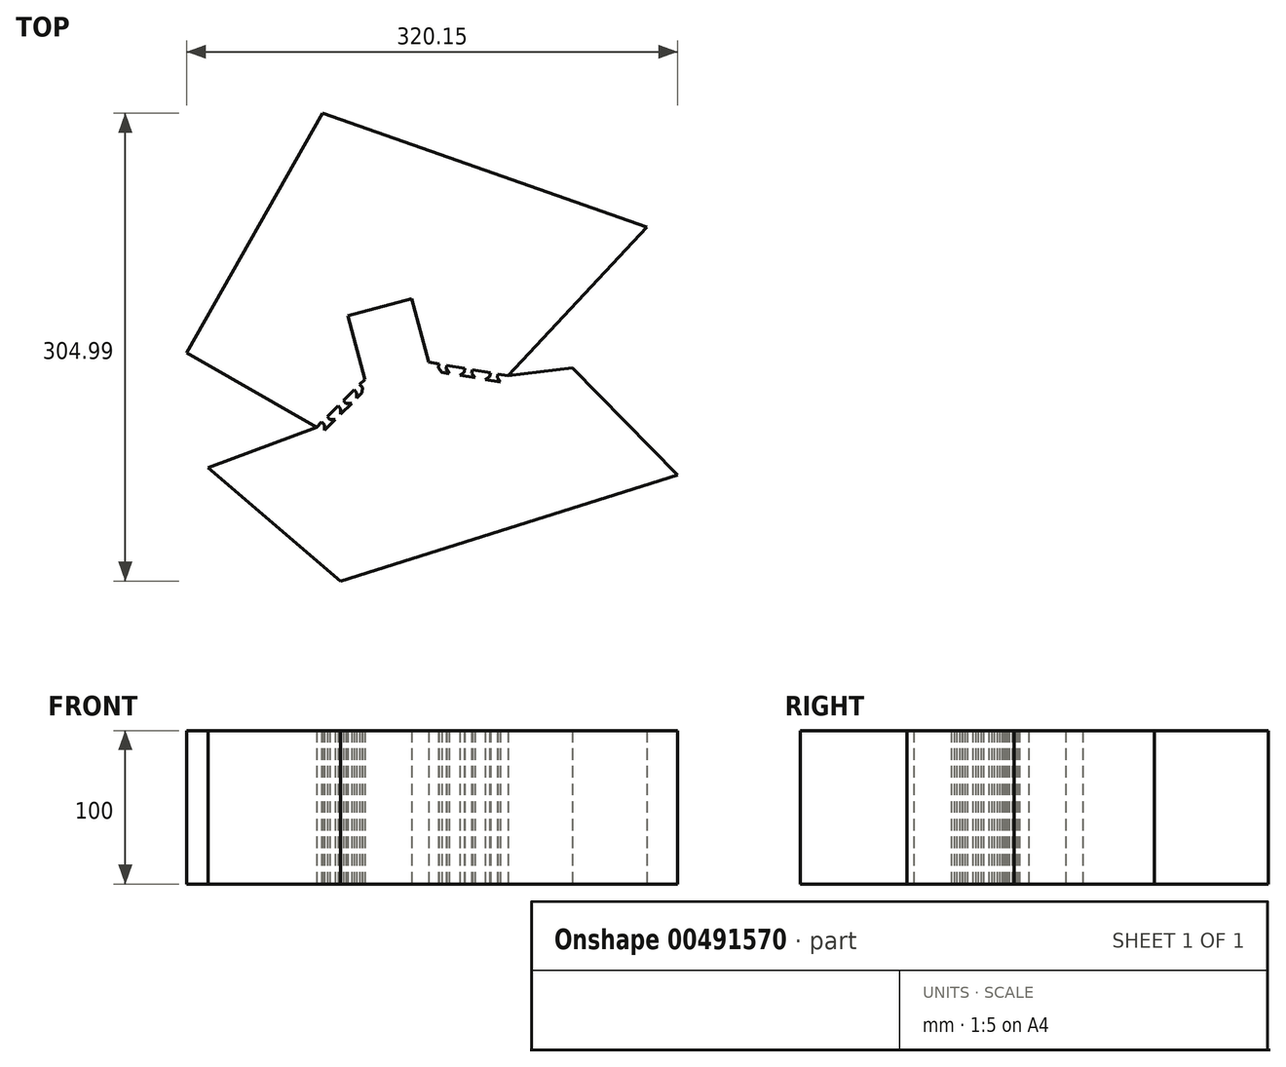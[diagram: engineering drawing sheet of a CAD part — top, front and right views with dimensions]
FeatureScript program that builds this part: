
annotation { "Feature Type Name" : "Feature", "Feature Type Description" : "" }
export const myFeature = defineFeature(function(context is Context, id is Id, definition is map)
    precondition{}
    {
        {
            var Q0;
            Q0=qCreatedBy(makeId("Top.planeOp"),FACE);
            var sketch = newSketch(context, id + "F0", { "sketchPlane" : qUnion([Q0])});
            skLineSegment(sketch, "E0", {"start": v(13.23, -95.22) * mm, "end": v(4.45, -92.87) * mm});
            skLineSegment(sketch, "E1", {"start": v(4.45, -92.87) * mm, "end": v(14.84, -54.1) * mm});
            skLineSegment(sketch, "E2", {"start": v(14.84, -54.1) * mm, "end": v(52.07, -64.07) * mm});
            skLineSegment(sketch, "E3", {"start": v(52.07, -64.07) * mm, "end": v(52.62, -63.48) * mm});
            skLineSegment(sketch, "E4", {"start": v(52.62, -63.48) * mm, "end": v(64.97, -66.78) * mm});
            skLineSegment(sketch, "E5", {"start": v(64.97, -66.78) * mm, "end": v(69.57, -49.62) * mm});
            skLineSegment(sketch, "E6", {"start": v(69.57, -49.62) * mm, "end": v(71.06, -48.58) * mm});
            skLineSegment(sketch, "E7", {"start": v(71.06, -48.58) * mm, "end": v(72.55, -48.7) * mm});
            skLineSegment(sketch, "E8", {"start": v(72.55, -48.7) * mm, "end": v(81.24, -48.85) * mm});
            skLineSegment(sketch, "E9", {"start": v(81.24, -48.85) * mm, "end": v(89.36, -48.18) * mm});
            skLineSegment(sketch, "E10", {"start": v(89.36, -48.18) * mm, "end": v(92.14, -47.5) * mm});
            skLineSegment(sketch, "E11", {"start": v(92.14, -47.5) * mm, "end": v(93.87, -41.05) * mm});
            skLineSegment(sketch, "E12", {"start": v(93.87, -41.05) * mm, "end": v(93.82, -41.03) * mm});
            skLineSegment(sketch, "E13", {"start": v(93.82, -41.03) * mm, "end": v(95.53, -34.66) * mm});
            skLineSegment(sketch, "E14", {"start": v(95.53, -34.66) * mm, "end": v(95.58, -34.67) * mm});
            skLineSegment(sketch, "E15", {"start": v(95.58, -34.67) * mm, "end": v(97.3, -28.22) * mm});
            skLineSegment(sketch, "E16", {"start": v(97.3, -28.22) * mm, "end": v(95.23, -26.24) * mm});
            skLineSegment(sketch, "E17", {"start": v(95.23, -26.24) * mm, "end": v(88.55, -21.6) * mm});
            skLineSegment(sketch, "E18", {"start": v(88.55, -21.6) * mm, "end": v(80.94, -17.38) * mm});
            skLineSegment(sketch, "E19", {"start": v(80.94, -17.38) * mm, "end": v(79.6, -16.74) * mm});
            skLineSegment(sketch, "E20", {"start": v(79.6, -16.74) * mm, "end": v(77.01, -11.2) * mm});
            skLineSegment(sketch, "E21", {"start": v(77.01, -11.2) * mm, "end": v(72.37, -13.37) * mm});
            skLineSegment(sketch, "E22", {"start": v(72.37, -13.37) * mm, "end": v(65.9, -10.6) * mm});
            skLineSegment(sketch, "E23", {"start": v(65.9, -10.6) * mm, "end": v(59.65, -8) * mm});
            skLineSegment(sketch, "E24", {"start": v(59.65, -8) * mm, "end": v(54.72, -5.74) * mm});
            skLineSegment(sketch, "E25", {"start": v(54.72, -5.74) * mm, "end": v(53.87, -5.26) * mm});
            skLineSegment(sketch, "E26", {"start": v(53.87, -5.26) * mm, "end": v(54.52, -3.42) * mm});
            skLineSegment(sketch, "E27", {"start": v(54.52, -3.42) * mm, "end": v(55.5, -0.95) * mm});
            skLineSegment(sketch, "E28", {"start": v(55.5, -0.95) * mm, "end": v(57.7, 4.32) * mm});
            skLineSegment(sketch, "E29", {"start": v(57.7, 4.32) * mm, "end": v(58.83, 7.13) * mm});
            skLineSegment(sketch, "E30", {"start": v(58.83, 7.13) * mm, "end": v(59.9, 10.04) * mm});
            skLineSegment(sketch, "E31", {"start": v(59.9, 10.04) * mm, "end": v(60.84, 13.05) * mm});
            skLineSegment(sketch, "E32", {"start": v(60.84, 13.05) * mm, "end": v(61.6, 16.13) * mm});
            skLineSegment(sketch, "E33", {"start": v(61.6, 16.13) * mm, "end": v(62.15, 19.25) * mm});
            skLineSegment(sketch, "E34", {"start": v(62.15, 19.25) * mm, "end": v(62.43, 22.38) * mm});
            skLineSegment(sketch, "E35", {"start": v(62.43, 22.38) * mm, "end": v(62.4, 25.48) * mm});
            skLineSegment(sketch, "E36", {"start": v(62.4, 25.48) * mm, "end": v(62.03, 28.51) * mm});
            skLineSegment(sketch, "E37", {"start": v(62.03, 28.51) * mm, "end": v(61.65, 30.08) * mm});
            skLineSegment(sketch, "E38", {"start": v(61.65, 30.08) * mm, "end": v(56.95, 31.97) * mm});
            skLineSegment(sketch, "E39", {"start": v(56.95, 31.97) * mm, "end": v(54.45, 32.5) * mm});
            skLineSegment(sketch, "E40", {"start": v(54.45, 32.5) * mm, "end": v(54.48, 32.63) * mm});
            skLineSegment(sketch, "E41", {"start": v(54.48, 32.63) * mm, "end": v(53.29, 33.7) * mm});
            skLineSegment(sketch, "E42", {"start": v(53.29, 33.7) * mm, "end": v(53.62, 35.26) * mm});
            skLineSegment(sketch, "E43", {"start": v(53.62, 35.26) * mm, "end": v(55.14, 35.76) * mm});
            skLineSegment(sketch, "E44", {"start": v(55.14, 35.76) * mm, "end": v(55.33, 35.6) * mm});
            skLineSegment(sketch, "E45", {"start": v(55.33, 35.6) * mm, "end": v(57.89, 35.05) * mm});
            skLineSegment(sketch, "E46", {"start": v(57.89, 35.05) * mm, "end": v(60.28, 34.08) * mm});
            skLineSegment(sketch, "E47", {"start": v(60.28, 34.08) * mm, "end": v(60.23, 34.2) * mm});
            skLineSegment(sketch, "E48", {"start": v(60.23, 34.2) * mm, "end": v(58.8, 36.78) * mm});
            skLineSegment(sketch, "E49", {"start": v(58.8, 36.78) * mm, "end": v(57.03, 39.14) * mm});
            skLineSegment(sketch, "E50", {"start": v(57.03, 39.14) * mm, "end": v(54.94, 41.25) * mm});
            skLineSegment(sketch, "E51", {"start": v(54.94, 41.25) * mm, "end": v(52.56, 43.1) * mm});
            skLineSegment(sketch, "E52", {"start": v(52.56, 43.1) * mm, "end": v(49.94, 44.66) * mm});
            skLineSegment(sketch, "E53", {"start": v(49.94, 44.66) * mm, "end": v(47.12, 45.96) * mm});
            skLineSegment(sketch, "E54", {"start": v(47.12, 45.96) * mm, "end": v(44.15, 46.98) * mm});
            skLineSegment(sketch, "E55", {"start": v(44.15, 46.98) * mm, "end": v(41.07, 47.75) * mm});
            skLineSegment(sketch, "E56", {"start": v(41.07, 47.75) * mm, "end": v(37.95, 48.3) * mm});
            skLineSegment(sketch, "E57", {"start": v(37.95, 48.3) * mm, "end": v(34.82, 48.66) * mm});
            skLineSegment(sketch, "E58", {"start": v(34.82, 48.66) * mm, "end": v(31.72, 48.87) * mm});
            skLineSegment(sketch, "E59", {"start": v(31.72, 48.87) * mm, "end": v(28.7, 48.99) * mm});
            skLineSegment(sketch, "E60", {"start": v(28.7, 48.99) * mm, "end": v(23, 49.11) * mm});
            skLineSegment(sketch, "E61", {"start": v(23, 49.11) * mm, "end": v(20.34, 49.22) * mm});
            skLineSegment(sketch, "E62", {"start": v(20.34, 49.22) * mm, "end": v(17.82, 49.43) * mm});
            skLineSegment(sketch, "E63", {"start": v(17.82, 49.43) * mm, "end": v(15.44, 49.77) * mm});
            skLineSegment(sketch, "E64", {"start": v(15.44, 49.77) * mm, "end": v(13.2, 50.28) * mm});
            skLineSegment(sketch, "E65", {"start": v(13.2, 50.28) * mm, "end": v(11.05, 50.98) * mm});
            skLineSegment(sketch, "E66", {"start": v(11.05, 50.98) * mm, "end": v(8.98, 51.9) * mm});
            skLineSegment(sketch, "E67", {"start": v(8.98, 51.9) * mm, "end": v(6.96, 53.02) * mm});
            skLineSegment(sketch, "E68", {"start": v(6.96, 53.02) * mm, "end": v(4.97, 54.36) * mm});
            skLineSegment(sketch, "E69", {"start": v(4.97, 54.36) * mm, "end": v(2.97, 55.9) * mm});
            skLineSegment(sketch, "E70", {"start": v(2.97, 55.9) * mm, "end": v(0.92, 57.59) * mm});
            skLineSegment(sketch, "E71", {"start": v(0.92, 57.59) * mm, "end": v(-3.4, 61.31) * mm});
            skLineSegment(sketch, "E72", {"start": v(-3.4, 61.31) * mm, "end": v(-5.73, 63.25) * mm});
            skLineSegment(sketch, "E73", {"start": v(-5.73, 63.25) * mm, "end": v(-8.17, 65.16) * mm});
            skLineSegment(sketch, "E74", {"start": v(-8.17, 65.16) * mm, "end": v(-10.74, 66.99) * mm});
            skLineSegment(sketch, "E75", {"start": v(-10.74, 66.99) * mm, "end": v(-13.4, 68.66) * mm});
            skLineSegment(sketch, "E76", {"start": v(-13.4, 68.66) * mm, "end": v(-16.2, 75.2) * mm});
            skLineSegment(sketch, "E77", {"start": v(-16.2, 75.2) * mm, "end": v(-14.04, 79.84) * mm});
            skLineSegment(sketch, "E78", {"start": v(-14.04, 79.84) * mm, "end": v(-19.57, 82.42) * mm});
            skLineSegment(sketch, "E79", {"start": v(-19.57, 82.42) * mm, "end": v(-20.2, 83.77) * mm});
            skLineSegment(sketch, "E80", {"start": v(-20.2, 83.77) * mm, "end": v(-24.43, 91.38) * mm});
            skLineSegment(sketch, "E81", {"start": v(-24.43, 91.38) * mm, "end": v(-29.07, 98.06) * mm});
            skLineSegment(sketch, "E82", {"start": v(-29.07, 98.06) * mm, "end": v(-31.05, 100.13) * mm});
            skLineSegment(sketch, "E83", {"start": v(-31.05, 100.13) * mm, "end": v(-37.5, 98.4) * mm});
            skLineSegment(sketch, "E84", {"start": v(-37.5, 98.4) * mm, "end": v(-37.49, 98.36) * mm});
            skLineSegment(sketch, "E85", {"start": v(-37.49, 98.36) * mm, "end": v(-43.86, 96.65) * mm});
            skLineSegment(sketch, "E86", {"start": v(-43.86, 96.65) * mm, "end": v(-43.88, 96.7) * mm});
            skLineSegment(sketch, "E87", {"start": v(-43.88, 96.7) * mm, "end": v(-50.32, 94.97) * mm});
            skLineSegment(sketch, "E88", {"start": v(-50.32, 94.97) * mm, "end": v(-51, 92.19) * mm});
            skLineSegment(sketch, "E89", {"start": v(-51, 92.19) * mm, "end": v(-51.68, 84.07) * mm});
            skLineSegment(sketch, "E90", {"start": v(-51.68, 84.07) * mm, "end": v(-51.53, 75.38) * mm});
            skLineSegment(sketch, "E91", {"start": v(-51.53, 75.38) * mm, "end": v(-51.4, 73.9) * mm});
            skLineSegment(sketch, "E92", {"start": v(-51.4, 73.9) * mm, "end": v(-54.91, 68.89) * mm});
            skLineSegment(sketch, "E93", {"start": v(-54.91, 68.89) * mm, "end": v(-50.4, 65.73) * mm});
            skLineSegment(sketch, "E94", {"start": v(-50.4, 65.73) * mm, "end": v(-48.9, 67.88) * mm});
            skLineSegment(sketch, "E95", {"start": v(-48.9, 67.88) * mm, "end": v(-42.35, 43.42) * mm});
            skLineSegment(sketch, "E96", {"start": v(-42.35, 43.42) * mm, "end": v(-51.04, 41.1) * mm});
            skLineSegment(sketch, "E97", {"start": v(-51.04, 41.1) * mm, "end": v(-53.64, 50.8) * mm});
            skLineSegment(sketch, "E98", {"start": v(-53.64, 50.8) * mm, "end": v(-53.81, 50.37) * mm});
            skLineSegment(sketch, "E99", {"start": v(-53.81, 50.37) * mm, "end": v(-54.85, 47.53) * mm});
            skLineSegment(sketch, "E100", {"start": v(-54.85, 47.53) * mm, "end": v(-56.74, 42.14) * mm});
            skLineSegment(sketch, "E101", {"start": v(-56.74, 42.14) * mm, "end": v(-57.66, 39.65) * mm});
            skLineSegment(sketch, "E102", {"start": v(-57.66, 39.65) * mm, "end": v(-58.63, 37.32) * mm});
            skLineSegment(sketch, "E103", {"start": v(-58.63, 37.32) * mm, "end": v(-59.7, 35.16) * mm});
            skLineSegment(sketch, "E104", {"start": v(-59.7, 35.16) * mm, "end": v(-60.87, 33.18) * mm});
            skLineSegment(sketch, "E105", {"start": v(-60.87, 33.18) * mm, "end": v(-62.2, 31.35) * mm});
            skLineSegment(sketch, "E106", {"start": v(-62.2, 31.35) * mm, "end": v(-63.71, 29.67) * mm});
            skLineSegment(sketch, "E107", {"start": v(-63.71, 29.67) * mm, "end": v(-65.4, 28.1) * mm});
            skLineSegment(sketch, "E108", {"start": v(-65.4, 28.1) * mm, "end": v(-67.3, 26.62) * mm});
            skLineSegment(sketch, "E109", {"start": v(-67.3, 26.62) * mm, "end": v(-69.37, 25.19) * mm});
            skLineSegment(sketch, "E110", {"start": v(-69.37, 25.19) * mm, "end": v(-71.62, 23.76) * mm});
            skLineSegment(sketch, "E111", {"start": v(-71.62, 23.76) * mm, "end": v(-76.5, 20.8) * mm});
            skLineSegment(sketch, "E112", {"start": v(-76.5, 20.8) * mm, "end": v(-79.06, 19.2) * mm});
            skLineSegment(sketch, "E113", {"start": v(-79.06, 19.2) * mm, "end": v(-81.63, 17.46) * mm});
            skLineSegment(sketch, "E114", {"start": v(-81.63, 17.46) * mm, "end": v(-84.16, 15.58) * mm});
            skLineSegment(sketch, "E115", {"start": v(-84.16, 15.58) * mm, "end": v(-86.6, 13.54) * mm});
            skLineSegment(sketch, "E116", {"start": v(-86.6, 13.54) * mm, "end": v(-88.87, 11.34) * mm});
            skLineSegment(sketch, "E117", {"start": v(-88.87, 11.34) * mm, "end": v(-90.93, 8.96) * mm});
            skLineSegment(sketch, "E118", {"start": v(-90.93, 8.96) * mm, "end": v(-92.73, 6.44) * mm});
            skLineSegment(sketch, "E119", {"start": v(-92.73, 6.44) * mm, "end": v(-94.22, 3.77) * mm});
            skLineSegment(sketch, "E120", {"start": v(-94.22, 3.77) * mm, "end": v(-94.82, 2.28) * mm});
            skLineSegment(sketch, "E121", {"start": v(-94.82, 2.28) * mm, "end": v(-92.14, -2.02) * mm});
            skLineSegment(sketch, "E122", {"start": v(-92.14, -2.02) * mm, "end": v(-90.43, -3.92) * mm});
            skLineSegment(sketch, "E123", {"start": v(-90.43, -3.92) * mm, "end": v(-90.52, -4) * mm});
            skLineSegment(sketch, "E124", {"start": v(-90.52, -4) * mm, "end": v(-90.19, -5.56) * mm});
            skLineSegment(sketch, "E125", {"start": v(-90.19, -5.56) * mm, "end": v(-91.38, -6.63) * mm});
            skLineSegment(sketch, "E126", {"start": v(-91.38, -6.63) * mm, "end": v(-92.9, -6.14) * mm});
            skLineSegment(sketch, "E127", {"start": v(-92.9, -6.14) * mm, "end": v(-92.95, -5.9) * mm});
            skLineSegment(sketch, "E128", {"start": v(-92.95, -5.9) * mm, "end": v(-94.7, -3.95) * mm});
            skLineSegment(sketch, "E129", {"start": v(-94.7, -3.95) * mm, "end": v(-96.07, -1.76) * mm});
            skLineSegment(sketch, "E130", {"start": v(-96.07, -1.76) * mm, "end": v(-96.1, -1.9) * mm});
            skLineSegment(sketch, "E131", {"start": v(-96.1, -1.9) * mm, "end": v(-96.46, -4.82) * mm});
            skLineSegment(sketch, "E132", {"start": v(-96.46, -4.82) * mm, "end": v(-96.41, -7.77) * mm});
            skLineSegment(sketch, "E133", {"start": v(-96.41, -7.77) * mm, "end": v(-95.96, -10.7) * mm});
            skLineSegment(sketch, "E134", {"start": v(-95.96, -10.7) * mm, "end": v(-95.13, -13.6) * mm});
            skLineSegment(sketch, "E135", {"start": v(-95.13, -13.6) * mm, "end": v(-93.93, -16.4) * mm});
            skLineSegment(sketch, "E136", {"start": v(-93.93, -16.4) * mm, "end": v(-92.4, -19.1) * mm});
            skLineSegment(sketch, "E137", {"start": v(-92.4, -19.1) * mm, "end": v(-90.6, -21.68) * mm});
            skLineSegment(sketch, "E138", {"start": v(-90.6, -21.68) * mm, "end": v(-88.57, -24.11) * mm});
            skLineSegment(sketch, "E139", {"start": v(-88.57, -24.11) * mm, "end": v(-86.36, -26.4) * mm});
            skLineSegment(sketch, "E140", {"start": v(-86.36, -26.4) * mm, "end": v(-84.04, -28.53) * mm});
            skLineSegment(sketch, "E141", {"start": v(-84.04, -28.53) * mm, "end": v(-81.66, -30.52) * mm});
            skLineSegment(sketch, "E142", {"start": v(-81.66, -30.52) * mm, "end": v(-79.29, -32.39) * mm});
            skLineSegment(sketch, "E143", {"start": v(-79.29, -32.39) * mm, "end": v(-74.74, -35.84) * mm});
            skLineSegment(sketch, "E144", {"start": v(-74.74, -35.84) * mm, "end": v(-72.66, -37.5) * mm});
            skLineSegment(sketch, "E145", {"start": v(-72.66, -37.5) * mm, "end": v(-71.18, -38.76) * mm});
            skLineSegment(sketch, "E146", {"start": v(-71.18, -38.76) * mm, "end": v(-71.67, -39.6) * mm});
            skLineSegment(sketch, "E147", {"start": v(-71.67, -39.6) * mm, "end": v(-74.81, -44.02) * mm});
            skLineSegment(sketch, "E148", {"start": v(-74.81, -44.02) * mm, "end": v(-78.92, -49.4) * mm});
            skLineSegment(sketch, "E149", {"start": v(-78.92, -49.4) * mm, "end": v(-83.14, -55.04) * mm});
            skLineSegment(sketch, "E150", {"start": v(-83.14, -55.04) * mm, "end": v(-88.24, -55.49) * mm});
            skLineSegment(sketch, "E151", {"start": v(-88.24, -55.49) * mm, "end": v(-87.7, -61.57) * mm});
            skLineSegment(sketch, "E152", {"start": v(-87.7, -61.57) * mm, "end": v(-88.56, -62.8) * mm});
            skLineSegment(sketch, "E153", {"start": v(-88.56, -62.8) * mm, "end": v(-93.03, -70.25) * mm});
            skLineSegment(sketch, "E154", {"start": v(-93.03, -70.25) * mm, "end": v(-96.5, -77.61) * mm});
            skLineSegment(sketch, "E155", {"start": v(-96.5, -77.61) * mm, "end": v(-97.3, -80.37) * mm});
            skLineSegment(sketch, "E156", {"start": v(-97.3, -80.37) * mm, "end": v(-92.58, -85.09) * mm});
            skLineSegment(sketch, "E157", {"start": v(-92.58, -85.09) * mm, "end": v(-92.55, -85.05) * mm});
            skLineSegment(sketch, "E158", {"start": v(-92.55, -85.05) * mm, "end": v(-87.88, -89.72) * mm});
            skLineSegment(sketch, "E159", {"start": v(-87.88, -89.72) * mm, "end": v(-87.92, -89.75) * mm});
            skLineSegment(sketch, "E160", {"start": v(-87.92, -89.75) * mm, "end": v(-83.2, -94.47) * mm});
            skLineSegment(sketch, "E161", {"start": v(-83.2, -94.47) * mm, "end": v(-80.44, -93.67) * mm});
            skLineSegment(sketch, "E162", {"start": v(-80.44, -93.67) * mm, "end": v(-73.08, -90.2) * mm});
            skLineSegment(sketch, "E163", {"start": v(-73.08, -90.2) * mm, "end": v(-65.63, -85.73) * mm});
            skLineSegment(sketch, "E164", {"start": v(-65.63, -85.73) * mm, "end": v(-64.4, -84.88) * mm});
            skLineSegment(sketch, "E165", {"start": v(-64.4, -84.88) * mm, "end": v(-58.32, -85.4) * mm});
            skLineSegment(sketch, "E166", {"start": v(-58.32, -85.4) * mm, "end": v(-57.87, -80.31) * mm});
            skLineSegment(sketch, "E167", {"start": v(-57.87, -80.31) * mm, "end": v(-54.33, -77.66) * mm});
            skLineSegment(sketch, "E168", {"start": v(-54.33, -77.66) * mm, "end": v(-53.76, -78.62) * mm});
            skLineSegment(sketch, "E169", {"start": v(-53.76, -78.62) * mm, "end": v(-51.9, -81.1) * mm});
            skLineSegment(sketch, "E170", {"start": v(-51.9, -81.1) * mm, "end": v(-49.83, -83.35) * mm});
            skLineSegment(sketch, "E171", {"start": v(-49.83, -83.35) * mm, "end": v(-48.6, -84.38) * mm});
            skLineSegment(sketch, "E172", {"start": v(-48.6, -84.38) * mm, "end": v(-43.69, -83.16) * mm});
            skLineSegment(sketch, "E173", {"start": v(-43.69, -83.16) * mm, "end": v(-41.35, -82.12) * mm});
            skLineSegment(sketch, "E174", {"start": v(-41.35, -82.12) * mm, "end": v(-41.3, -82.23) * mm});
            skLineSegment(sketch, "E175", {"start": v(-41.3, -82.23) * mm, "end": v(-39.71, -82.4) * mm});
            skLineSegment(sketch, "E176", {"start": v(-39.71, -82.4) * mm, "end": v(-39.06, -83.86) * mm});
            skLineSegment(sketch, "E177", {"start": v(-39.06, -83.86) * mm, "end": v(-40, -85.16) * mm});
            skLineSegment(sketch, "E178", {"start": v(-40, -85.16) * mm, "end": v(-40.25, -85.13) * mm});
            skLineSegment(sketch, "E179", {"start": v(-40.25, -85.13) * mm, "end": v(-42.64, -86.2) * mm});
            skLineSegment(sketch, "E180", {"start": v(-42.64, -86.2) * mm, "end": v(-45.15, -86.82) * mm});
            skLineSegment(sketch, "E181", {"start": v(-45.15, -86.82) * mm, "end": v(-45.03, -86.9) * mm});
            skLineSegment(sketch, "E182", {"start": v(-45.03, -86.9) * mm, "end": v(-42.36, -88.14) * mm});
            skLineSegment(sketch, "E183", {"start": v(-42.36, -88.14) * mm, "end": v(-39.54, -89) * mm});
            skLineSegment(sketch, "E184", {"start": v(-39.54, -89) * mm, "end": v(-36.6, -89.48) * mm});
            skLineSegment(sketch, "E185", {"start": v(-36.6, -89.48) * mm, "end": v(-33.6, -89.58) * mm});
            skLineSegment(sketch, "E186", {"start": v(-33.6, -89.58) * mm, "end": v(-30.56, -89.3) * mm});
            skLineSegment(sketch, "E187", {"start": v(-30.56, -89.3) * mm, "end": v(-27.52, -88.7) * mm});
            skLineSegment(sketch, "E188", {"start": v(-27.52, -88.7) * mm, "end": v(-24.5, -87.77) * mm});
            skLineSegment(sketch, "E189", {"start": v(-24.5, -87.77) * mm, "end": v(-21.57, -86.59) * mm});
            skLineSegment(sketch, "E190", {"start": v(-21.57, -86.59) * mm, "end": v(-18.72, -85.2) * mm});
            skLineSegment(sketch, "E191", {"start": v(-18.72, -85.2) * mm, "end": v(-15.97, -83.65) * mm});
            skLineSegment(sketch, "E192", {"start": v(-15.97, -83.65) * mm, "end": v(-13.34, -82) * mm});
            skLineSegment(sketch, "E193", {"start": v(-13.34, -82) * mm, "end": v(-10.83, -80.32) * mm});
            skLineSegment(sketch, "E194", {"start": v(-10.83, -80.32) * mm, "end": v(-6.14, -77.06) * mm});
            skLineSegment(sketch, "E195", {"start": v(-6.14, -77.06) * mm, "end": v(-3.93, -75.6) * mm});
            skLineSegment(sketch, "E196", {"start": v(-3.93, -75.6) * mm, "end": v(-1.89, -74.35) * mm});
            skLineSegment(sketch, "E197", {"start": v(-1.89, -74.35) * mm, "end": v(-7.4, -94.96) * mm});
            skLineSegment(sketch, "E198", {"start": v(-7.4, -94.96) * mm, "end": v(11.9, -100.13) * mm});
            skLineSegment(sketch, "E199", {"start": v(11.9, -100.13) * mm, "end": v(13.23, -95.22) * mm});
            skLineSegment(sketch, "E200", {"start": v(-41.07, 86.22) * mm, "end": v(-40.95, 86.25) * mm});
            skLineSegment(sketch, "E201", {"start": v(-40.95, 86.25) * mm, "end": v(-41, 86.4) * mm});
            skLineSegment(sketch, "E202", {"start": v(-41, 86.4) * mm, "end": v(-40.82, 86.6) * mm});
            skLineSegment(sketch, "E203", {"start": v(-40.82, 86.6) * mm, "end": v(-40.84, 86.65) * mm});
            skLineSegment(sketch, "E204", {"start": v(-40.84, 86.65) * mm, "end": v(-40.6, 86.96) * mm});
            skLineSegment(sketch, "E205", {"start": v(-40.6, 86.96) * mm, "end": v(-40.35, 87.03) * mm});
            skLineSegment(sketch, "E206", {"start": v(-40.35, 87.03) * mm, "end": v(-40.38, 87.13) * mm});
            skLineSegment(sketch, "E207", {"start": v(-40.38, 87.13) * mm, "end": v(-40.05, 87.5) * mm});
            skLineSegment(sketch, "E208", {"start": v(-40.05, 87.5) * mm, "end": v(-39.59, 87.77) * mm});
            skLineSegment(sketch, "E209", {"start": v(-39.59, 87.77) * mm, "end": v(-39.3, 86.7) * mm});
            skLineSegment(sketch, "E210", {"start": v(-39.3, 86.7) * mm, "end": v(-36.46, 87.46) * mm});
            skLineSegment(sketch, "E211", {"start": v(-36.46, 87.46) * mm, "end": v(-36.75, 88.53) * mm});
            skLineSegment(sketch, "E212", {"start": v(-36.75, 88.53) * mm, "end": v(-36.74, 88.53) * mm});
            skLineSegment(sketch, "E213", {"start": v(-36.74, 88.53) * mm, "end": v(-36.58, 88.55) * mm});
            skLineSegment(sketch, "E214", {"start": v(-36.58, 88.55) * mm, "end": v(-35.94, 88.47) * mm});
            skLineSegment(sketch, "E215", {"start": v(-35.94, 88.47) * mm, "end": v(-35.7, 88.27) * mm});
            skLineSegment(sketch, "E216", {"start": v(-35.7, 88.27) * mm, "end": v(-35.47, 88.34) * mm});
            skLineSegment(sketch, "E217", {"start": v(-35.47, 88.34) * mm, "end": v(-35.06, 88.17) * mm});
            skLineSegment(sketch, "E218", {"start": v(-35.06, 88.17) * mm, "end": v(-35.06, 88.15) * mm});
            skLineSegment(sketch, "E219", {"start": v(-35.06, 88.15) * mm, "end": v(-34.77, 87.91) * mm});
            skLineSegment(sketch, "E220", {"start": v(-34.77, 87.91) * mm, "end": v(-34.7, 87.93) * mm});
            skLineSegment(sketch, "E221", {"start": v(-34.7, 87.93) * mm, "end": v(-32.05, 78.07) * mm});
            skLineSegment(sketch, "E222", {"start": v(-32.05, 78.07) * mm, "end": v(-38.43, 76.36) * mm});
            skLineSegment(sketch, "E223", {"start": v(-38.43, 76.36) * mm, "end": v(-41.07, 86.22) * mm});
            skLineSegment(sketch, "E224", {"start": v(22.96, 40.54) * mm, "end": v(23.69, 41.96) * mm});
            skLineSegment(sketch, "E225", {"start": v(23.69, 41.96) * mm, "end": v(23.8, 41.97) * mm});
            skLineSegment(sketch, "E226", {"start": v(23.8, 41.97) * mm, "end": v(25.7, 43.2) * mm});
            skLineSegment(sketch, "E227", {"start": v(25.7, 43.2) * mm, "end": v(29.94, 45.36) * mm});
            skLineSegment(sketch, "E228", {"start": v(29.94, 45.36) * mm, "end": v(34.37, 47.06) * mm});
            skLineSegment(sketch, "E229", {"start": v(34.37, 47.06) * mm, "end": v(36.66, 47.67) * mm});
            skLineSegment(sketch, "E230", {"start": v(36.66, 47.67) * mm, "end": v(37.49, 44.58) * mm});
            skLineSegment(sketch, "E231", {"start": v(37.49, 44.58) * mm, "end": v(35.36, 44.01) * mm});
            skLineSegment(sketch, "E232", {"start": v(35.36, 44.01) * mm, "end": v(31.24, 42.43) * mm});
            skLineSegment(sketch, "E233", {"start": v(31.24, 42.43) * mm, "end": v(27.31, 40.43) * mm});
            skLineSegment(sketch, "E234", {"start": v(27.31, 40.43) * mm, "end": v(25.46, 39.23) * mm});
            skLineSegment(sketch, "E235", {"start": v(25.46, 39.23) * mm, "end": v(25.43, 39.28) * mm});
            skLineSegment(sketch, "E236", {"start": v(25.43, 39.28) * mm, "end": v(23.83, 39.2) * mm});
            skLineSegment(sketch, "E237", {"start": v(23.83, 39.2) * mm, "end": v(22.96, 40.54) * mm});
            skLineSegment(sketch, "E238", {"start": v(-50.75, 33.92) * mm, "end": v(-9.15, 45.07) * mm});
            skLineSegment(sketch, "E239", {"start": v(-9.15, 45.07) * mm, "end": v(1.98, 3.54) * mm});
            skLineSegment(sketch, "E240", {"start": v(1.94, 3.5) * mm, "end": v(-39.66, -7.65) * mm});
            skLineSegment(sketch, "E241", {"start": v(-39.62, -7.6) * mm, "end": v(-50.75, 33.92) * mm});
            skLineSegment(sketch, "E242", {"start": v(32.15, 6.18) * mm, "end": v(28.9, 7.43) * mm});
            skLineSegment(sketch, "E243", {"start": v(28.9, 7.43) * mm, "end": v(25.98, 9.33) * mm});
            skLineSegment(sketch, "E244", {"start": v(25.98, 9.33) * mm, "end": v(23.52, 11.8) * mm});
            skLineSegment(sketch, "E245", {"start": v(23.52, 11.8) * mm, "end": v(21.62, 14.71) * mm});
            skLineSegment(sketch, "E246", {"start": v(21.62, 14.71) * mm, "end": v(20.37, 17.97) * mm});
            skLineSegment(sketch, "E247", {"start": v(20.37, 17.97) * mm, "end": v(19.82, 21.4) * mm});
            skLineSegment(sketch, "E248", {"start": v(19.82, 21.4) * mm, "end": v(20, 24.89) * mm});
            skLineSegment(sketch, "E249", {"start": v(20, 24.89) * mm, "end": v(20.9, 28.25) * mm});
            skLineSegment(sketch, "E250", {"start": v(20.9, 28.25) * mm, "end": v(22.5, 31.36) * mm});
            skLineSegment(sketch, "E251", {"start": v(22.5, 31.36) * mm, "end": v(24.68, 34.06) * mm});
            skLineSegment(sketch, "E252", {"start": v(24.68, 34.06) * mm, "end": v(27.4, 36.26) * mm});
            skLineSegment(sketch, "E253", {"start": v(27.4, 36.26) * mm, "end": v(30.5, 37.84) * mm});
            skLineSegment(sketch, "E254", {"start": v(30.5, 37.84) * mm, "end": v(33.86, 38.74) * mm});
            skLineSegment(sketch, "E255", {"start": v(33.86, 38.74) * mm, "end": v(37.34, 38.92) * mm});
            skLineSegment(sketch, "E256", {"start": v(37.34, 38.92) * mm, "end": v(40.78, 38.38) * mm});
            skLineSegment(sketch, "E257", {"start": v(40.78, 38.38) * mm, "end": v(44.03, 37.13) * mm});
            skLineSegment(sketch, "E258", {"start": v(44.03, 37.13) * mm, "end": v(46.96, 35.23) * mm});
            skLineSegment(sketch, "E259", {"start": v(46.96, 35.23) * mm, "end": v(49.42, 32.77) * mm});
            skLineSegment(sketch, "E260", {"start": v(49.42, 32.77) * mm, "end": v(51.32, 29.85) * mm});
            skLineSegment(sketch, "E261", {"start": v(51.32, 29.85) * mm, "end": v(52.57, 26.6) * mm});
            skLineSegment(sketch, "E262", {"start": v(52.57, 26.6) * mm, "end": v(53.11, 23.15) * mm});
            skLineSegment(sketch, "E263", {"start": v(53.11, 23.15) * mm, "end": v(52.93, 19.67) * mm});
            skLineSegment(sketch, "E264", {"start": v(52.93, 19.67) * mm, "end": v(52.03, 16.3) * mm});
            skLineSegment(sketch, "E265", {"start": v(52.03, 16.3) * mm, "end": v(50.45, 13.2) * mm});
            skLineSegment(sketch, "E266", {"start": v(50.45, 13.2) * mm, "end": v(48.25, 10.5) * mm});
            skLineSegment(sketch, "E267", {"start": v(48.25, 10.5) * mm, "end": v(45.55, 8.3) * mm});
            skLineSegment(sketch, "E268", {"start": v(45.55, 8.3) * mm, "end": v(42.44, 6.72) * mm});
            skLineSegment(sketch, "E269", {"start": v(42.44, 6.72) * mm, "end": v(39.08, 5.82) * mm});
            skLineSegment(sketch, "E270", {"start": v(39.08, 5.82) * mm, "end": v(35.6, 5.64) * mm});
            skLineSegment(sketch, "E271", {"start": v(35.6, 5.64) * mm, "end": v(32.15, 6.18) * mm});
            skLineSegment(sketch, "E272", {"start": v(-70.15, 14.9) * mm, "end": v(-70.07, 16.5) * mm});
            skLineSegment(sketch, "E273", {"start": v(-70.07, 16.5) * mm, "end": v(-68.64, 17.22) * mm});
            skLineSegment(sketch, "E274", {"start": v(-68.64, 17.22) * mm, "end": v(-67.3, 16.35) * mm});
            skLineSegment(sketch, "E275", {"start": v(-67.3, 16.35) * mm, "end": v(-67.38, 14.76) * mm});
            skLineSegment(sketch, "E276", {"start": v(-67.38, 14.76) * mm, "end": v(-68.8, 14.03) * mm});
            skLineSegment(sketch, "E277", {"start": v(-68.8, 14.03) * mm, "end": v(-70.15, 14.9) * mm});
            skLineSegment(sketch, "E278", {"start": v(-74.18, -22.31) * mm, "end": v(-77.44, -21.06) * mm});
            skLineSegment(sketch, "E279", {"start": v(-77.44, -21.06) * mm, "end": v(-80.36, -19.17) * mm});
            skLineSegment(sketch, "E280", {"start": v(-80.36, -19.17) * mm, "end": v(-82.82, -16.7) * mm});
            skLineSegment(sketch, "E281", {"start": v(-82.82, -16.7) * mm, "end": v(-84.72, -13.78) * mm});
            skLineSegment(sketch, "E282", {"start": v(-84.72, -13.78) * mm, "end": v(-85.97, -10.53) * mm});
            skLineSegment(sketch, "E283", {"start": v(-85.97, -10.53) * mm, "end": v(-86.51, -7.09) * mm});
            skLineSegment(sketch, "E284", {"start": v(-86.51, -7.09) * mm, "end": v(-86.33, -3.6) * mm});
            skLineSegment(sketch, "E285", {"start": v(-86.33, -3.6) * mm, "end": v(-85.43, -0.24) * mm});
            skLineSegment(sketch, "E286", {"start": v(-85.43, -0.24) * mm, "end": v(-83.85, 2.86) * mm});
            skLineSegment(sketch, "E287", {"start": v(-83.85, 2.86) * mm, "end": v(-81.66, 5.57) * mm});
            skLineSegment(sketch, "E288", {"start": v(-81.66, 5.57) * mm, "end": v(-78.95, 7.76) * mm});
            skLineSegment(sketch, "E289", {"start": v(-78.95, 7.76) * mm, "end": v(-75.84, 9.35) * mm});
            skLineSegment(sketch, "E290", {"start": v(-75.84, 9.35) * mm, "end": v(-72.48, 10.25) * mm});
            skLineSegment(sketch, "E291", {"start": v(-72.48, 10.25) * mm, "end": v(-69, 10.43) * mm});
            skLineSegment(sketch, "E292", {"start": v(-69, 10.43) * mm, "end": v(-65.56, 9.89) * mm});
            skLineSegment(sketch, "E293", {"start": v(-65.56, 9.89) * mm, "end": v(-62.3, 8.64) * mm});
            skLineSegment(sketch, "E294", {"start": v(-62.3, 8.64) * mm, "end": v(-59.38, 6.74) * mm});
            skLineSegment(sketch, "E295", {"start": v(-59.38, 6.74) * mm, "end": v(-56.92, 4.28) * mm});
            skLineSegment(sketch, "E296", {"start": v(-56.92, 4.28) * mm, "end": v(-55.02, 1.35) * mm});
            skLineSegment(sketch, "E297", {"start": v(-55.02, 1.35) * mm, "end": v(-53.77, -1.9) * mm});
            skLineSegment(sketch, "E298", {"start": v(-53.77, -1.9) * mm, "end": v(-53.23, -5.34) * mm});
            skLineSegment(sketch, "E299", {"start": v(-53.23, -5.34) * mm, "end": v(-53.4, -8.82) * mm});
            skLineSegment(sketch, "E300", {"start": v(-53.4, -8.82) * mm, "end": v(-54.31, -12.19) * mm});
            skLineSegment(sketch, "E301", {"start": v(-54.31, -12.19) * mm, "end": v(-55.9, -15.3) * mm});
            skLineSegment(sketch, "E302", {"start": v(-55.9, -15.3) * mm, "end": v(-58.09, -18) * mm});
            skLineSegment(sketch, "E303", {"start": v(-58.09, -18) * mm, "end": v(-60.8, -20.2) * mm});
            skLineSegment(sketch, "E304", {"start": v(-60.8, -20.2) * mm, "end": v(-63.9, -21.77) * mm});
            skLineSegment(sketch, "E305", {"start": v(-63.9, -21.77) * mm, "end": v(-67.26, -22.67) * mm});
            skLineSegment(sketch, "E306", {"start": v(-67.26, -22.67) * mm, "end": v(-70.74, -22.86) * mm});
            skLineSegment(sketch, "E307", {"start": v(-70.74, -22.86) * mm, "end": v(-74.18, -22.31) * mm});
            skLineSegment(sketch, "E308", {"start": v(46.78, 3.85) * mm, "end": v(47.5, 5.28) * mm});
            skLineSegment(sketch, "E309", {"start": v(47.5, 5.28) * mm, "end": v(49.1, 5.36) * mm});
            skLineSegment(sketch, "E310", {"start": v(49.1, 5.36) * mm, "end": v(49.98, 4.02) * mm});
            skLineSegment(sketch, "E311", {"start": v(49.98, 4.02) * mm, "end": v(49.25, 2.6) * mm});
            skLineSegment(sketch, "E312", {"start": v(49.25, 2.6) * mm, "end": v(47.65, 2.51) * mm});
            skLineSegment(sketch, "E313", {"start": v(47.65, 2.51) * mm, "end": v(46.78, 3.85) * mm});
            skLineSegment(sketch, "E314", {"start": v(-7.36, -2.45) * mm, "end": v(1.34, -0.12) * mm});
            skLineSegment(sketch, "E315", {"start": v(1.34, -0.12) * mm, "end": v(9.1, -29.1) * mm});
            skLineSegment(sketch, "E316", {"start": v(9.1, -29.1) * mm, "end": v(0.4, -31.42) * mm});
            skLineSegment(sketch, "E317", {"start": v(0.4, -31.42) * mm, "end": v(-7.36, -2.45) * mm});
            skLineSegment(sketch, "E318", {"start": v(-13.22, -11.23) * mm, "end": v(-14.3, -9.84) * mm});
            skLineSegment(sketch, "E319", {"start": v(-14.3, -9.84) * mm, "end": v(-14.06, -8.1) * mm});
            skLineSegment(sketch, "E320", {"start": v(-14.06, -8.1) * mm, "end": v(-12.67, -7.02) * mm});
            skLineSegment(sketch, "E321", {"start": v(-12.67, -7.02) * mm, "end": v(-10.92, -7.25) * mm});
            skLineSegment(sketch, "E322", {"start": v(-10.92, -7.25) * mm, "end": v(-9.85, -8.65) * mm});
            skLineSegment(sketch, "E323", {"start": v(-9.85, -8.65) * mm, "end": v(-10.08, -10.4) * mm});
            skLineSegment(sketch, "E324", {"start": v(-10.08, -10.4) * mm, "end": v(-11.48, -11.46) * mm});
            skLineSegment(sketch, "E325", {"start": v(-11.48, -11.46) * mm, "end": v(-13.22, -11.23) * mm});
            skLineSegment(sketch, "E326", {"start": v(-37.23, -10.45) * mm, "end": v(-28.54, -8.12) * mm});
            skLineSegment(sketch, "E327", {"start": v(-28.54, -8.12) * mm, "end": v(-20.77, -37.1) * mm});
            skLineSegment(sketch, "E328", {"start": v(-20.77, -37.1) * mm, "end": v(-29.47, -39.43) * mm});
            skLineSegment(sketch, "E329", {"start": v(-29.47, -39.43) * mm, "end": v(-37.23, -10.45) * mm});
            skLineSegment(sketch, "E330", {"start": v(59.63, -53.3) * mm, "end": v(25.72, -44.22) * mm});
            skLineSegment(sketch, "E331", {"start": v(25.72, -44.22) * mm, "end": v(24.95, -47.11) * mm});
            skLineSegment(sketch, "E332", {"start": v(24.95, -47.11) * mm, "end": v(16.25, -44.78) * mm});
            skLineSegment(sketch, "E333", {"start": v(16.25, -44.78) * mm, "end": v(25.05, -11.94) * mm});
            skLineSegment(sketch, "E334", {"start": v(25.05, -11.94) * mm, "end": v(63.69, -22.3) * mm});
            skLineSegment(sketch, "E335", {"start": v(63.69, -22.3) * mm, "end": v(62.67, -42.73) * mm});
            skLineSegment(sketch, "E336", {"start": v(62.67, -42.73) * mm, "end": v(62.18, -45.7) * mm});
            skLineSegment(sketch, "E337", {"start": v(62.18, -45.7) * mm, "end": v(59.63, -53.3) * mm});
            skLineSegment(sketch, "E338", {"start": v(-71.2, -29.58) * mm, "end": v(-73.47, -29.47) * mm});
            skLineSegment(sketch, "E339", {"start": v(-73.47, -29.47) * mm, "end": v(-78.15, -28.72) * mm});
            skLineSegment(sketch, "E340", {"start": v(-78.15, -28.72) * mm, "end": v(-82.74, -27.5) * mm});
            skLineSegment(sketch, "E341", {"start": v(-82.74, -27.5) * mm, "end": v(-84.95, -26.64) * mm});
            skLineSegment(sketch, "E342", {"start": v(-84.95, -26.64) * mm, "end": v(-83.8, -23.66) * mm});
            skLineSegment(sketch, "E343", {"start": v(-83.8, -23.66) * mm, "end": v(-81.75, -24.45) * mm});
            skLineSegment(sketch, "E344", {"start": v(-81.75, -24.45) * mm, "end": v(-77.49, -25.59) * mm});
            skLineSegment(sketch, "E345", {"start": v(-77.49, -25.59) * mm, "end": v(-73.13, -26.28) * mm});
            skLineSegment(sketch, "E346", {"start": v(-73.13, -26.28) * mm, "end": v(-70.93, -26.4) * mm});
            skLineSegment(sketch, "E347", {"start": v(-70.93, -26.4) * mm, "end": v(-70.93, -26.46) * mm});
            skLineSegment(sketch, "E348", {"start": v(-70.93, -26.46) * mm, "end": v(-69.59, -27.33) * mm});
            skLineSegment(sketch, "E349", {"start": v(-69.59, -27.33) * mm, "end": v(-69.67, -28.93) * mm});
            skLineSegment(sketch, "E350", {"start": v(-69.67, -28.93) * mm, "end": v(-71.1, -29.65) * mm});
            skLineSegment(sketch, "E351", {"start": v(-71.1, -29.65) * mm, "end": v(-71.2, -29.58) * mm});
            skLineSegment(sketch, "E352", {"start": v(73.54, -35.6) * mm, "end": v(75.24, -29.22) * mm});
            skLineSegment(sketch, "E353", {"start": v(75.24, -29.22) * mm, "end": v(85.1, -31.86) * mm});
            skLineSegment(sketch, "E354", {"start": v(85.1, -31.86) * mm, "end": v(85.07, -31.98) * mm});
            skLineSegment(sketch, "E355", {"start": v(85.07, -31.98) * mm, "end": v(85.22, -32.02) * mm});
            skLineSegment(sketch, "E356", {"start": v(85.22, -32.02) * mm, "end": v(85.3, -32.27) * mm});
            skLineSegment(sketch, "E357", {"start": v(85.3, -32.27) * mm, "end": v(85.36, -32.28) * mm});
            skLineSegment(sketch, "E358", {"start": v(85.36, -32.28) * mm, "end": v(85.5, -32.64) * mm});
            skLineSegment(sketch, "E359", {"start": v(85.5, -32.64) * mm, "end": v(85.44, -32.89) * mm});
            skLineSegment(sketch, "E360", {"start": v(85.44, -32.89) * mm, "end": v(85.55, -32.92) * mm});
            skLineSegment(sketch, "E361", {"start": v(85.55, -32.92) * mm, "end": v(85.7, -33.39) * mm});
            skLineSegment(sketch, "E362", {"start": v(85.7, -33.39) * mm, "end": v(85.7, -33.92) * mm});
            skLineSegment(sketch, "E363", {"start": v(85.7, -33.92) * mm, "end": v(84.63, -33.63) * mm});
            skLineSegment(sketch, "E364", {"start": v(84.63, -33.63) * mm, "end": v(83.87, -36.47) * mm});
            skLineSegment(sketch, "E365", {"start": v(83.87, -36.47) * mm, "end": v(84.94, -36.76) * mm});
            skLineSegment(sketch, "E366", {"start": v(84.94, -36.76) * mm, "end": v(84.94, -36.77) * mm});
            skLineSegment(sketch, "E367", {"start": v(84.94, -36.77) * mm, "end": v(84.87, -36.92) * mm});
            skLineSegment(sketch, "E368", {"start": v(84.87, -36.92) * mm, "end": v(84.48, -37.43) * mm});
            skLineSegment(sketch, "E369", {"start": v(84.48, -37.43) * mm, "end": v(84.2, -37.54) * mm});
            skLineSegment(sketch, "E370", {"start": v(84.2, -37.54) * mm, "end": v(84.13, -37.77) * mm});
            skLineSegment(sketch, "E371", {"start": v(84.13, -37.77) * mm, "end": v(83.78, -38.04) * mm});
            skLineSegment(sketch, "E372", {"start": v(83.78, -38.04) * mm, "end": v(83.76, -38.03) * mm});
            skLineSegment(sketch, "E373", {"start": v(83.76, -38.03) * mm, "end": v(83.41, -38.16) * mm});
            skLineSegment(sketch, "E374", {"start": v(83.41, -38.16) * mm, "end": v(83.4, -38.24) * mm});
            skLineSegment(sketch, "E375", {"start": v(83.4, -38.24) * mm, "end": v(73.54, -35.6) * mm});
            skLineSegment(sketch, "E376", {"start": v(-37.13, -79.37) * mm, "end": v(-40.38, -78.13) * mm});
            skLineSegment(sketch, "E377", {"start": v(-40.38, -78.13) * mm, "end": v(-43.3, -76.23) * mm});
            skLineSegment(sketch, "E378", {"start": v(-43.3, -76.23) * mm, "end": v(-45.77, -73.76) * mm});
            skLineSegment(sketch, "E379", {"start": v(-45.77, -73.76) * mm, "end": v(-47.66, -70.84) * mm});
            skLineSegment(sketch, "E380", {"start": v(-47.66, -70.84) * mm, "end": v(-48.91, -67.59) * mm});
            skLineSegment(sketch, "E381", {"start": v(-48.91, -67.59) * mm, "end": v(-49.46, -64.15) * mm});
            skLineSegment(sketch, "E382", {"start": v(-49.46, -64.15) * mm, "end": v(-49.28, -60.67) * mm});
            skLineSegment(sketch, "E383", {"start": v(-49.28, -60.67) * mm, "end": v(-48.37, -57.3) * mm});
            skLineSegment(sketch, "E384", {"start": v(-48.37, -57.3) * mm, "end": v(-46.8, -54.2) * mm});
            skLineSegment(sketch, "E385", {"start": v(-46.8, -54.2) * mm, "end": v(-44.6, -51.5) * mm});
            skLineSegment(sketch, "E386", {"start": v(-44.6, -51.5) * mm, "end": v(-41.9, -49.3) * mm});
            skLineSegment(sketch, "E387", {"start": v(-41.9, -49.3) * mm, "end": v(-38.79, -47.72) * mm});
            skLineSegment(sketch, "E388", {"start": v(-38.79, -47.72) * mm, "end": v(-35.42, -46.81) * mm});
            skLineSegment(sketch, "E389", {"start": v(-35.42, -46.81) * mm, "end": v(-31.94, -46.63) * mm});
            skLineSegment(sketch, "E390", {"start": v(-31.94, -46.63) * mm, "end": v(-28.5, -47.18) * mm});
            skLineSegment(sketch, "E391", {"start": v(-28.5, -47.18) * mm, "end": v(-25.25, -48.43) * mm});
            skLineSegment(sketch, "E392", {"start": v(-25.25, -48.43) * mm, "end": v(-22.33, -50.32) * mm});
            skLineSegment(sketch, "E393", {"start": v(-22.33, -50.32) * mm, "end": v(-19.86, -52.79) * mm});
            skLineSegment(sketch, "E394", {"start": v(-19.86, -52.79) * mm, "end": v(-17.96, -55.7) * mm});
            skLineSegment(sketch, "E395", {"start": v(-17.96, -55.7) * mm, "end": v(-16.72, -58.96) * mm});
            skLineSegment(sketch, "E396", {"start": v(-16.72, -58.96) * mm, "end": v(-16.17, -62.4) * mm});
            skLineSegment(sketch, "E397", {"start": v(-16.17, -62.4) * mm, "end": v(-16.35, -65.88) * mm});
            skLineSegment(sketch, "E398", {"start": v(-16.35, -65.88) * mm, "end": v(-17.25, -69.25) * mm});
            skLineSegment(sketch, "E399", {"start": v(-17.25, -69.25) * mm, "end": v(-18.84, -72.35) * mm});
            skLineSegment(sketch, "E400", {"start": v(-18.84, -72.35) * mm, "end": v(-21.03, -75.06) * mm});
            skLineSegment(sketch, "E401", {"start": v(-21.03, -75.06) * mm, "end": v(-23.74, -77.25) * mm});
            skLineSegment(sketch, "E402", {"start": v(-23.74, -77.25) * mm, "end": v(-26.84, -78.84) * mm});
            skLineSegment(sketch, "E403", {"start": v(-26.84, -78.84) * mm, "end": v(-30.2, -79.74) * mm});
            skLineSegment(sketch, "E404", {"start": v(-30.2, -79.74) * mm, "end": v(-33.69, -79.92) * mm});
            skLineSegment(sketch, "E405", {"start": v(-33.69, -79.92) * mm, "end": v(-37.13, -79.37) * mm});
            skLineSegment(sketch, "E406", {"start": v(-54.47, -56.45) * mm, "end": v(-54.72, -54.87) * mm});
            skLineSegment(sketch, "E407", {"start": v(-54.72, -54.87) * mm, "end": v(-53.48, -53.86) * mm});
            skLineSegment(sketch, "E408", {"start": v(-53.48, -53.86) * mm, "end": v(-51.99, -54.43) * mm});
            skLineSegment(sketch, "E409", {"start": v(-51.99, -54.43) * mm, "end": v(-51.74, -56.01) * mm});
            skLineSegment(sketch, "E410", {"start": v(-51.74, -56.01) * mm, "end": v(-52.98, -57.02) * mm});
            skLineSegment(sketch, "E411", {"start": v(-52.98, -57.02) * mm, "end": v(-54.47, -56.45) * mm});
            skLineSegment(sketch, "E412", {"start": v(-20.53, -81.92) * mm, "end": v(-19.14, -80.2) * mm});
            skLineSegment(sketch, "E413", {"start": v(-19.14, -80.2) * mm, "end": v(-16.74, -76.5) * mm});
            skLineSegment(sketch, "E414", {"start": v(-16.74, -76.5) * mm, "end": v(-14.74, -72.58) * mm});
            skLineSegment(sketch, "E415", {"start": v(-14.74, -72.58) * mm, "end": v(-13.95, -70.52) * mm});
            skLineSegment(sketch, "E416", {"start": v(-13.95, -70.52) * mm, "end": v(-13.9, -70.54) * mm});
            skLineSegment(sketch, "E417", {"start": v(-13.9, -70.54) * mm, "end": v(-12.65, -69.53) * mm});
            skLineSegment(sketch, "E418", {"start": v(-12.65, -69.53) * mm, "end": v(-11.15, -70.1) * mm});
            skLineSegment(sketch, "E419", {"start": v(-11.15, -70.1) * mm, "end": v(-10.9, -71.69) * mm});
            skLineSegment(sketch, "E420", {"start": v(-10.9, -71.69) * mm, "end": v(-11, -71.77) * mm});
            skLineSegment(sketch, "E421", {"start": v(-11, -71.77) * mm, "end": v(-11.81, -73.88) * mm});
            skLineSegment(sketch, "E422", {"start": v(-11.81, -73.88) * mm, "end": v(-13.97, -78.1) * mm});
            skLineSegment(sketch, "E423", {"start": v(-13.97, -78.1) * mm, "end": v(-16.55, -82.09) * mm});
            skLineSegment(sketch, "E424", {"start": v(-16.55, -82.09) * mm, "end": v(-18.04, -83.93) * mm});
            skLineSegment(sketch, "E425", {"start": v(-18.04, -83.93) * mm, "end": v(-20.53, -81.92) * mm});
            skLineSegment(sketch, "E426", {"start": v(-80.7, -82.06) * mm, "end": v(-80.74, -82.1) * mm});
            skLineSegment(sketch, "E427", {"start": v(-80.74, -82.1) * mm, "end": v(-81.12, -82.05) * mm});
            skLineSegment(sketch, "E428", {"start": v(-81.12, -82.05) * mm, "end": v(-81.3, -81.87) * mm});
            skLineSegment(sketch, "E429", {"start": v(-81.3, -81.87) * mm, "end": v(-81.38, -81.94) * mm});
            skLineSegment(sketch, "E430", {"start": v(-81.38, -81.94) * mm, "end": v(-81.87, -81.84) * mm});
            skLineSegment(sketch, "E431", {"start": v(-81.87, -81.84) * mm, "end": v(-82.33, -81.58) * mm});
            skLineSegment(sketch, "E432", {"start": v(-82.33, -81.58) * mm, "end": v(-81.55, -80.8) * mm});
            skLineSegment(sketch, "E433", {"start": v(-81.55, -80.8) * mm, "end": v(-83.62, -78.71) * mm});
            skLineSegment(sketch, "E434", {"start": v(-83.62, -78.71) * mm, "end": v(-84.41, -79.5) * mm});
            skLineSegment(sketch, "E435", {"start": v(-84.41, -79.5) * mm, "end": v(-84.42, -79.5) * mm});
            skLineSegment(sketch, "E436", {"start": v(-84.42, -79.5) * mm, "end": v(-84.5, -79.36) * mm});
            skLineSegment(sketch, "E437", {"start": v(-84.5, -79.36) * mm, "end": v(-84.76, -78.77) * mm});
            skLineSegment(sketch, "E438", {"start": v(-84.76, -78.77) * mm, "end": v(-84.71, -78.46) * mm});
            skLineSegment(sketch, "E439", {"start": v(-84.71, -78.46) * mm, "end": v(-84.88, -78.3) * mm});
            skLineSegment(sketch, "E440", {"start": v(-84.88, -78.3) * mm, "end": v(-84.94, -77.86) * mm});
            skLineSegment(sketch, "E441", {"start": v(-84.94, -77.86) * mm, "end": v(-84.92, -77.84) * mm});
            skLineSegment(sketch, "E442", {"start": v(-84.92, -77.84) * mm, "end": v(-84.86, -77.47) * mm});
            skLineSegment(sketch, "E443", {"start": v(-84.86, -77.47) * mm, "end": v(-84.92, -77.42) * mm});
            skLineSegment(sketch, "E444", {"start": v(-84.92, -77.42) * mm, "end": v(-77.7, -70.2) * mm});
            skLineSegment(sketch, "E445", {"start": v(-77.7, -70.2) * mm, "end": v(-73.03, -74.87) * mm});
            skLineSegment(sketch, "E446", {"start": v(-73.03, -74.87) * mm, "end": v(-80.25, -82.09) * mm});
            skLineSegment(sketch, "E447", {"start": v(-80.25, -82.09) * mm, "end": v(-80.34, -82) * mm});
            skLineSegment(sketch, "E448", {"start": v(-80.34, -82) * mm, "end": v(-80.45, -82.11) * mm});
            skLineSegment(sketch, "E449", {"start": v(-80.45, -82.11) * mm, "end": v(-80.7, -82.06) * mm});
            skLineSegment(sketch, "E450", {"start": v(53.87, -5.26) * mm, "end": v(47.06, -4.1) * mm});
            skLineSegment(sketch, "E451", {"start": v(27.93, -0.86) * mm, "end": v(27.1, -5.79) * mm, "construction": true});
            skLineSegment(sketch, "E452", {"start": v(27.1, -5.79) * mm, "end": v(22.16, -4.95) * mm});
            skLineSegment(sketch, "E453", {"start": v(27.1, -5.79) * mm, "end": v(32.02, -6.62) * mm});
            skLineSegment(sketch, "E454", {"start": v(25.05, -2.9) * mm, "end": v(25.46, -0.44) * mm});
            skLineSegment(sketch, "E455", {"start": v(29.98, -3.74) * mm, "end": v(30.4, -1.28) * mm});
            skLineSegment(sketch, "E456", {"start": v(22.16, -4.95) * mm, "end": v(25.05, -2.9) * mm});
            skLineSegment(sketch, "E457", {"start": v(32.02, -6.62) * mm, "end": v(29.98, -3.74) * mm});
            skPoint(sketch, "E458.orphan", {"position": v(24.63, -5.37) * mm});
            skPoint(sketch, "E459.orphan", {"position": v(29.56, -6.2) * mm});
            skLineSegment(sketch, "E460.trimOffspring", {"start": v(8.8, 2.39) * mm, "end": v(1.98, 3.54) * mm});
            skLineSegment(sketch, "E461", {"start": v(13.72, 1.55) * mm, "end": v(12.88, -3.42) * mm, "construction": true});
            skLineSegment(sketch, "E462", {"start": v(13.72, 1.55) * mm, "end": v(25.46, -0.44) * mm});
            skLineSegment(sketch, "E463", {"start": v(19.6, 0.56) * mm, "end": v(18.89, -3.6) * mm, "construction": true});
            skLineSegment(sketch, "E464.MirrorCS", {"start": v(13.3, -0.91) * mm, "end": v(13.72, 1.55) * mm});
            skLineSegment(sketch, "E465.MirrorCS", {"start": v(15.35, -3.8) * mm, "end": v(13.3, -0.91) * mm});
            skLineSegment(sketch, "E466.MirrorCS", {"start": v(10.42, -2.96) * mm, "end": v(15.35, -3.8) * mm});
            skLineSegment(sketch, "E467.MirrorCS", {"start": v(8.37, -0.08) * mm, "end": v(8.8, 2.39) * mm});
            skLineSegment(sketch, "E468", {"start": v(42.13, -3.27) * mm, "end": v(41.15, -9.05) * mm, "construction": true});
            skLineSegment(sketch, "E469", {"start": v(30.4, -1.28) * mm, "end": v(42.13, -3.27) * mm});
            skLineSegment(sketch, "E470", {"start": v(36.26, -2.27) * mm, "end": v(35.56, -6.4) * mm, "construction": true});
            skLineSegment(sketch, "E471.MirrorCS", {"start": v(46.65, -6.57) * mm, "end": v(47.06, -4.1) * mm});
            skLineSegment(sketch, "E472.MirrorCS", {"start": v(48.7, -9.45) * mm, "end": v(46.65, -6.57) * mm});
            skLineSegment(sketch, "E473.MirrorCS", {"start": v(43.76, -8.61) * mm, "end": v(48.7, -9.45) * mm});
            skLineSegment(sketch, "E474.MirrorCS", {"start": v(43.76, -8.61) * mm, "end": v(38.83, -7.78) * mm});
            skLineSegment(sketch, "E475.MirrorCS", {"start": v(38.83, -7.78) * mm, "end": v(41.72, -5.73) * mm});
            skLineSegment(sketch, "E476.MirrorCS", {"start": v(41.72, -5.73) * mm, "end": v(42.13, -3.27) * mm});
            skLineSegment(sketch, "E477", {"start": v(-55.4, -23.18) * mm, "end": v(-51.89, -26.74) * mm, "construction": true});
            skLineSegment(sketch, "E478", {"start": v(-51.89, -26.74) * mm, "end": v(-48.33, -23.23) * mm});
            skLineSegment(sketch, "E479.MirrorCS", {"start": v(-51.89, -26.74) * mm, "end": v(-55.44, -30.26) * mm});
            skLineSegment(sketch, "E480", {"start": v(-55.44, -30.26) * mm, "end": v(-58.96, -26.7) * mm, "construction": true});
            skLineSegment(sketch, "E481", {"start": v(-48.33, -23.23) * mm, "end": v(-51.84, -19.67) * mm, "construction": true});
            skLineSegment(sketch, "E482", {"start": v(-55.44, -26.74) * mm, "end": v(-51.89, -23.23) * mm, "construction": true});
            skLineSegment(sketch, "E483", {"start": v(-55.44, -30.26) * mm, "end": v(-55.44, -26.74) * mm});
            skLineSegment(sketch, "E484", {"start": v(-55.44, -26.74) * mm, "end": v(-57.2, -24.96) * mm});
            skLineSegment(sketch, "E485", {"start": v(-48.33, -23.23) * mm, "end": v(-51.89, -23.23) * mm});
            skLineSegment(sketch, "E486", {"start": v(-51.89, -23.23) * mm, "end": v(-53.64, -21.45) * mm});
            skPoint(sketch, "E487.orphan", {"position": v(-57.2, -28.48) * mm});
            skPoint(sketch, "E488.orphan", {"position": v(-50.08, -21.45) * mm});
            skLineSegment(sketch, "E489", {"start": v(-64.19, -31.86) * mm, "end": v(-61.24, -34.85) * mm, "construction": true});
            skLineSegment(sketch, "E490", {"start": v(-46.63, -14.53) * mm, "end": v(-43.03, -18.18) * mm, "construction": true});
            skLineSegment(sketch, "E491.trimOffspring", {"start": v(-43.07, -11.02) * mm, "end": v(-39.62, -7.6) * mm});
            skLineSegment(sketch, "E492", {"start": v(-57.2, -24.96) * mm, "end": v(-64.19, -31.86) * mm});
            skLineSegment(sketch, "E493", {"start": v(-53.64, -21.45) * mm, "end": v(-46.63, -14.53) * mm});
            skLineSegment(sketch, "E494", {"start": v(-71.18, -38.76) * mm, "end": v(-67.75, -35.38) * mm});
            skLineSegment(sketch, "E495", {"start": v(-60.7, -28.41) * mm, "end": v(-58.32, -30.81) * mm, "construction": true});
            skLineSegment(sketch, "E496", {"start": v(-50.14, -17.99) * mm, "end": v(-47.46, -20.7) * mm, "construction": true});
            skLineSegment(sketch, "E497.MirrorCS", {"start": v(-62.43, -33.64) * mm, "end": v(-64.19, -31.86) * mm});
            skLineSegment(sketch, "E498.MirrorCS", {"start": v(-58.92, -33.69) * mm, "end": v(-62.43, -33.64) * mm});
            skLineSegment(sketch, "E499.MirrorCS", {"start": v(-62.48, -37.2) * mm, "end": v(-58.92, -33.69) * mm});
            skLineSegment(sketch, "E500.MirrorCS", {"start": v(-62.48, -37.2) * mm, "end": v(-66.04, -40.71) * mm});
            skLineSegment(sketch, "E501.MirrorCS", {"start": v(-66.04, -40.71) * mm, "end": v(-66, -37.15) * mm});
            skLineSegment(sketch, "E502.MirrorCS", {"start": v(-66, -37.15) * mm, "end": v(-67.75, -35.38) * mm});
            skLineSegment(sketch, "E503.MirrorCS", {"start": v(-41.32, -12.8) * mm, "end": v(-43.07, -11.02) * mm});
            skLineSegment(sketch, "E504.MirrorCS", {"start": v(-41.36, -16.35) * mm, "end": v(-44.92, -19.87) * mm});
            skLineSegment(sketch, "E505.MirrorCS", {"start": v(-44.92, -19.87) * mm, "end": v(-44.87, -16.3) * mm});
            skLineSegment(sketch, "E506.MirrorCS", {"start": v(-44.87, -16.3) * mm, "end": v(-46.63, -14.53) * mm});
            skLineSegment(sketch, "E507", {"start": v(-41.36, -16.35) * mm, "end": v(-41.32, -12.8) * mm});
            skPoint(sketch, "E508.MirrorCS.end.orphan", {"position": v(-41.32, -12.8) * mm});
            skPoint(sketch, "E508.MirrorCS.start.orphan", {"position": v(-37.8, -12.84) * mm});
            skLineSegment(sketch, "E509", {"start": v(10.42, -2.96) * mm, "end": v(8.37, -0.08) * mm});
            skPoint(sketch, "E510.MirrorCS.start.orphan", {"position": v(5.5, -2.13) * mm});
            skPoint(sketch, "E511.MirrorCS.start.orphan", {"position": v(10.42, -2.96) * mm});
            skLineSegment(sketch, "E512", {"start": v(-71.18, -38.76) * mm, "end": v(-141.86, -65.22) * mm});
            skLineSegment(sketch, "E513", {"start": v(-141.86, -65.22) * mm, "end": v(-55.36, -139.13) * mm});
            skLineSegment(sketch, "E514", {"start": v(-55.36, -139.13) * mm, "end": v(164.33, -69.85) * mm});
            skLineSegment(sketch, "E515", {"start": v(164.33, -69.85) * mm, "end": v(95.57, 0) * mm});
            skLineSegment(sketch, "E516", {"start": v(95.57, 0) * mm, "end": v(53.87, -5.26) * mm});
            skLineSegment(sketch, "E517", {"start": v(53.87, -5.26) * mm, "end": v(144.17, 91.62) * mm});
            skLineSegment(sketch, "E518", {"start": v(144.17, 91.62) * mm, "end": v(-67.26, 165.86) * mm});
            skLineSegment(sketch, "E519", {"start": v(-67.26, 165.86) * mm, "end": v(-155.82, 9.69) * mm});
            skLineSegment(sketch, "E520", {"start": v(-155.82, 9.69) * mm, "end": v(-71.18, -38.76) * mm});
            skSolve(sketch);
        }
        {
            var Q0;
            Q0=makeQuery(id+"F0.imprint","IMPRINT",FACE,{"disambiguationData":[TD([[makeQuery(id+"F0.imprint","IMPRINT",EDGE,{"derivedFrom":sQuery(id+"F0.wireOp",EDGE,"E26")}),1.0]])]});
            var Q1;
            Q1=makeQuery(id+"F0.imprint","IMPRINT",FACE,{"disambiguationData":[TD([[makeQuery(id+"F0.imprint","IMPRINT",EDGE,{"derivedFrom":sQuery(id+"F0.wireOp",EDGE,"E200")}),-1.0]])]});
            var Q2;
            Q2=makeQuery(id+"F0.imprint","IMPRINT",FACE,{"disambiguationData":[TD([[makeQuery(id+"F0.imprint","IMPRINT",EDGE,{"derivedFrom":sQuery(id+"F0.wireOp",EDGE,"E242")}),-1.0]])]});
            var Q3;
            Q3=makeQuery(id+"F0.imprint","IMPRINT",FACE,{"disambiguationData":[TD([[makeQuery(id+"F0.imprint","IMPRINT",EDGE,{"derivedFrom":sQuery(id+"F0.wireOp",EDGE,"E278")}),-1.0]])]});
            var Q4;
            Q4=makeQuery(id+"F0.imprint","IMPRINT",FACE,{"disambiguationData":[TD([[makeQuery(id+"F0.imprint","IMPRINT",EDGE,{"derivedFrom":sQuery(id+"F0.wireOp",EDGE,"E272")}),-1.0]])]});
            var Q5;
            Q5=makeQuery(id+"F0.imprint","IMPRINT",FACE,{"disambiguationData":[TD([[makeQuery(id+"F0.imprint","IMPRINT",EDGE,{"derivedFrom":sQuery(id+"F0.wireOp",EDGE,"E308")}),-1.0]])]});
            var Q6;
            Q6=makeQuery(id+"F0.imprint","IMPRINT",FACE,{"disambiguationData":[TD([[makeQuery(id+"F0.imprint","IMPRINT",EDGE,{"derivedFrom":sQuery(id+"F0.wireOp",EDGE,"E224")}),-1.0]])]});
            var Q7;
            Q7=makeQuery(id+"F0.imprint","IMPRINT",FACE,{"disambiguationData":[TD([[makeQuery(id+"F0.imprint","IMPRINT",EDGE,{"derivedFrom":sQuery(id+"F0.wireOp",EDGE,"E338")}),-1.0]])]});
            var Q8;
            Q8=makeQuery(id+"F0.imprint","IMPRINT",FACE,{"disambiguationData":[TD([[makeQuery(id+"F0.imprint","IMPRINT",EDGE,{"derivedFrom":sQuery(id+"F0.wireOp",EDGE,"E26")}),-1.0]])]});
            extrude(context, id + "F1", {"entities" : qUnion([Q0, Q1, Q2, Q3, Q4, Q5, Q6, Q7, Q8]), "depth" : 100 * mm, "offsetDistance" : 25 * mm});
        }
        {
            var Q0;
            Q0=makeQuery(id+"F0.imprint","IMPRINT",FACE,{"disambiguationData":[TD([[makeQuery(id+"F0.imprint","IMPRINT",EDGE,{"derivedFrom":sQuery(id+"F0.wireOp",EDGE,"E0")}),1.0]])]});
            var Q1;
            Q1=makeQuery(id+"F0.imprint","IMPRINT",FACE,{"disambiguationData":[TD([[makeQuery(id+"F0.imprint","IMPRINT",EDGE,{"derivedFrom":sQuery(id+"F0.wireOp",EDGE,"E376")}),-1.0]])]});
            var Q2;
            Q2=makeQuery(id+"F0.imprint","IMPRINT",FACE,{"disambiguationData":[TD([[makeQuery(id+"F0.imprint","IMPRINT",EDGE,{"derivedFrom":sQuery(id+"F0.wireOp",EDGE,"E326")}),-1.0]])]});
            var Q3;
            Q3=makeQuery(id+"F0.imprint","IMPRINT",FACE,{"disambiguationData":[TD([[makeQuery(id+"F0.imprint","IMPRINT",EDGE,{"derivedFrom":sQuery(id+"F0.wireOp",EDGE,"E314")}),-1.0]])]});
            var Q4;
            Q4=makeQuery(id+"F0.imprint","IMPRINT",FACE,{"disambiguationData":[TD([[makeQuery(id+"F0.imprint","IMPRINT",EDGE,{"derivedFrom":sQuery(id+"F0.wireOp",EDGE,"E330")}),-1.0]])]});
            var Q5;
            Q5=makeQuery(id+"F0.imprint","IMPRINT",FACE,{"disambiguationData":[TD([[makeQuery(id+"F0.imprint","IMPRINT",EDGE,{"derivedFrom":sQuery(id+"F0.wireOp",EDGE,"E426")}),-1.0]])]});
            var Q6;
            Q6=makeQuery(id+"F0.imprint","IMPRINT",FACE,{"disambiguationData":[TD([[makeQuery(id+"F0.imprint","IMPRINT",EDGE,{"derivedFrom":sQuery(id+"F0.wireOp",EDGE,"E352")}),-1.0]])]});
            var Q7;
            Q7=makeQuery(id+"F0.imprint","IMPRINT",FACE,{"disambiguationData":[TD([[makeQuery(id+"F0.imprint","IMPRINT",EDGE,{"derivedFrom":sQuery(id+"F0.wireOp",EDGE,"E412")}),-1.0]])]});
            var Q8;
            Q8=makeQuery(id+"F0.imprint","IMPRINT",FACE,{"disambiguationData":[TD([[makeQuery(id+"F0.imprint","IMPRINT",EDGE,{"derivedFrom":sQuery(id+"F0.wireOp",EDGE,"E318")}),-1.0]])]});
            var Q9;
            Q9=makeQuery(id+"F0.imprint","IMPRINT",FACE,{"disambiguationData":[TD([[makeQuery(id+"F0.imprint","IMPRINT",EDGE,{"derivedFrom":sQuery(id+"F0.wireOp",EDGE,"E406")}),-1.0]])]});
            var Q10;
            Q10=makeQuery(id+"F0.imprint","IMPRINT",FACE,{"disambiguationData":[TD([[makeQuery(id+"F0.imprint","IMPRINT",EDGE,{"derivedFrom":sQuery(id+"F0.wireOp",EDGE,"E0")}),-1.0]])]});
            extrude(context, id + "F2", {"entities" : qUnion([Q0, Q1, Q2, Q3, Q4, Q5, Q6, Q7, Q8, Q9, Q10]), "depth" : 100 * mm, "offsetDistance" : 25 * mm});
        }
    });
